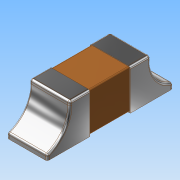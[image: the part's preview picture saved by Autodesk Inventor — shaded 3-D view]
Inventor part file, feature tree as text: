
AUTODESK INVENTOR PART (.ipt)
format: ipt  version: 2016 (Build 200138000, 138)  size: 203,776 bytes
history: native  units: mm
features: extrude x3, fillet x3, sketch x2, mirror x1, projected_geometry x1
ambient origin geometry x8: Origin, YZ Plane, XZ Plane, XY Plane, X Axis, Y Axis, Z Axis, Center Point
bodies: Body1 (feature_tree)
feature tree (10):
  extrude  "Extrusion4"  Depth=0.775mm
  sketch  "Sketch11"  dims[d9=0.775mm d10=0.0mm d12=0.4mm d13=0.0mm d14=0.1mm d15=0.85mm d16=0.0mm d17=0.65mm d18=0.0425mm d19=0.03mm d20=0.0125mm]
  extrude  "Extrusion5"  Depth=0.4mm TaperAngle=0.0deg
  extrude  "Extrusion6"  Depth=0.0125mm
  fillet  "Fillet1"  Radius=0.85mm
  fillet  "Fillet2"  Radius=0.65mm
  mirror  "Mirror1"
  fillet  "Fillet3"  Radius=0.0425mm
  sketch  "Sketch10"  dims[d7=0.8mm d8=0.775mm]
  projected_geometry  "Projected Loop1"
